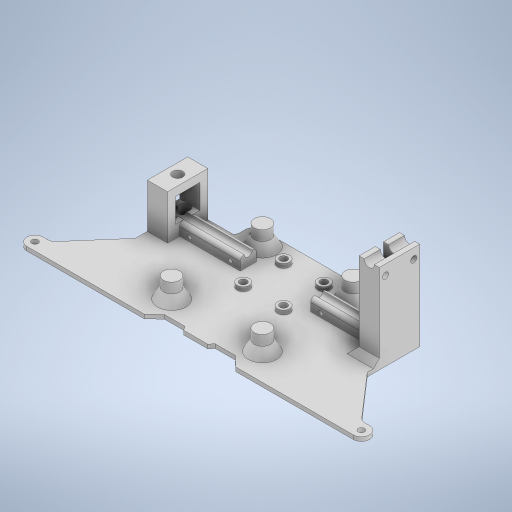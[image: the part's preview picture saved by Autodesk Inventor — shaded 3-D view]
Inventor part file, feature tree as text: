
AUTODESK INVENTOR PART (.ipt)
format: ipt  version: 2023 (Build 270158000, 158)  size: 628,736 bytes
history: native  units: in
note: dims shown in document units (in); Inventor stores cm internally (conversion verified against a paired STEP export)
features: extrude x20, sketch x20, chamfer x2, fillet x1
ambient origin geometry x8: Origin, YZ Plane, XZ Plane, XY Plane, X Axis, Y Axis, Z Axis, Center Point
bodies: Solid1 (feature_tree)
feature tree (43):
  extrude  "Extrusion1"  Depth=0.0984in
  extrude  "Extrusion2"  Depth=0.315in
  extrude  "Extrusion3"  Depth=2.3622in
  extrude  "Extrusion4"  Depth=0.0787in TaperAngle=0.0deg
  extrude  "Extrusion5"  Depth=0.315in
  extrude  "Extrusion6"  Depth=0.315in
  extrude  "Extrusion7"  Depth=1.7717in
  extrude  "Extrusion8"  Depth=1.7717in
  extrude  "Extrusion9"  Depth=1.7717in
  extrude  "Extrusion10"  Depth=0.3937in TaperAngle=0.0deg
  extrude  "Extrusion11"  Depth=0.7874in
  extrude  "Extrusion12"  Depth=0.2362in
  fillet  "Fillet1"  Radius=0.2362in
  extrude  "Extrusion13"  Depth=0.2362in
  sketch  "Sketch14"  dims[d48=2.6575in d49=0.9843in]
  chamfer  "Chamfer1"  Distance=0.0787in
  extrude  "Extrusion15"  Depth=0.9843in
  sketch  "Sketch16"  dims[d51=2.3622in]
  chamfer  "Chamfer2"  Distance=0.0787in
  extrude  "Extrusion17"  Depth=2.6575in
  extrude  "Extrusion18"  Depth=0.3937in TaperAngle=0.0deg
  extrude  "Extrusion20"  Depth=0.3937in
  extrude  "Extrusion21"  Depth=0.3937in
  extrude  "Extrusion22"  Depth=0.3937in
  extrude  "Extrusion23"  Depth=0.3937in
  sketch  "Sketch1"  dims[d0=0.0984in d1=0.0984in d2=0.1181in d3=0.1181in d4=0.315in]
  sketch  "Sketch2"  dims[d5=0.315in d6=0.315in]
  sketch  "Sketch3"  dims[d7=0.315in d8=2.3622in]
  sketch  "Sketch4"  dims[d18=0.1575in d19=0.0787in d20=0.0in]
  sketch  "Sketch5"  dims[d21=2.3622in d22=0.315in]
  sketch  "Sketch6"  dims[d23=0.315in d24=0.315in]
  sketch  "Sketch7"  dims[d25=0.315in d26=1.7717in]
  sketch  "Sketch8"  dims[d27=1.7717in d28=1.7717in]
  sketch  "Sketch9"  dims[d29=0.2756in d30=1.7717in]
  sketch  "Sketch10"  dims[d31=0.2953in d36=0.3937in d37=0.0in]
  sketch  "Sketch11"  dims[d38=0.1575in d39=0.0in d40=0.7874in]
  sketch  "Sketch12"  dims[d41=0.7874in d42=0.2362in d43=0.2362in]
  sketch  "Sketch13"  dims[d44=0.2362in d45=0.2362in d46=0.0787in d47=0.0in]
  sketch  "Sketch15"  dims[d50=1.1811in]
  sketch  "Sketch17"  dims[d52=0.7874in]
  sketch  "Sketch19"  dims[d53=0.1969in d54=0.0787in d55=0.0in]
  sketch  "Sketch20"  dims[d56=0.0787in d57=0.0in d58=2.6575in]
  sketch  "Sketch21"  dims[d61=0.0787in d62=0.0in d63=0.0787in d64=0.0in d65=0.9843in d66=1.1811in d67=0.3937in d68=0.7874in d69=1.6535in d70=0.0in d71=0.315in d72=0.1575in d73=1.5748in d74=0.2953in d75=0.0in d76=0.1969in d77=0.1969in d78=0.2953in d79=0.0in d80=0.1969in d81=0.1181in d82=0.5512in d83=0.1181in d84=0.1181in d85=0.3937in d86=0.0in d87=0.0787in d88=1.1811in d89=0.315in d90=0.2362in d91=0.0in d92=0.0787in d93=0.0787in d94=0.0in d95=0.0787in d96=0.0787in d97=0.1969in d98=0.7874in d99=0.2362in d100=0.0in d101=0.3937in d102=0.7874in d105=0.1181in d106=0.0787in d107=45.0deg d108=0.1378in d109=0.1378in d110=0.1378in d111=0.1378in d112=0.1181in d113=0.0in d114=0.2402in d115=0.1378in d116=0.1969in d117=0.1969in d118=1.6614in d119=0.2402in d122=0.1181in d123=0.1969in d124=45.0deg d125=0.1969in d126=0.1969in d127=0.0787in d128=0.0in d129=0.0787in d130=0.0in d138=0.2953in d139=0.2362in d140=1.5748in d141=0.315in d142=0.8661in d143=0.0in d144=0.4724in d145=0.4724in d146=0.1575in d147=0.1575in d148=0.8661in d149=0.0in d150=0.3937in d151=0.3937in d152=0.4724in d153=0.1575in d154=0.0in d155=0.1969in d156=0.1969in d157=0.0984in d158=0.0984in d159=0.3937in d160=0.0in d161=0.1969in d162=0.7874in d163=0.0787in d164=0.0787in d165=0.1969in d166=0.3937in d167=0.0in]
